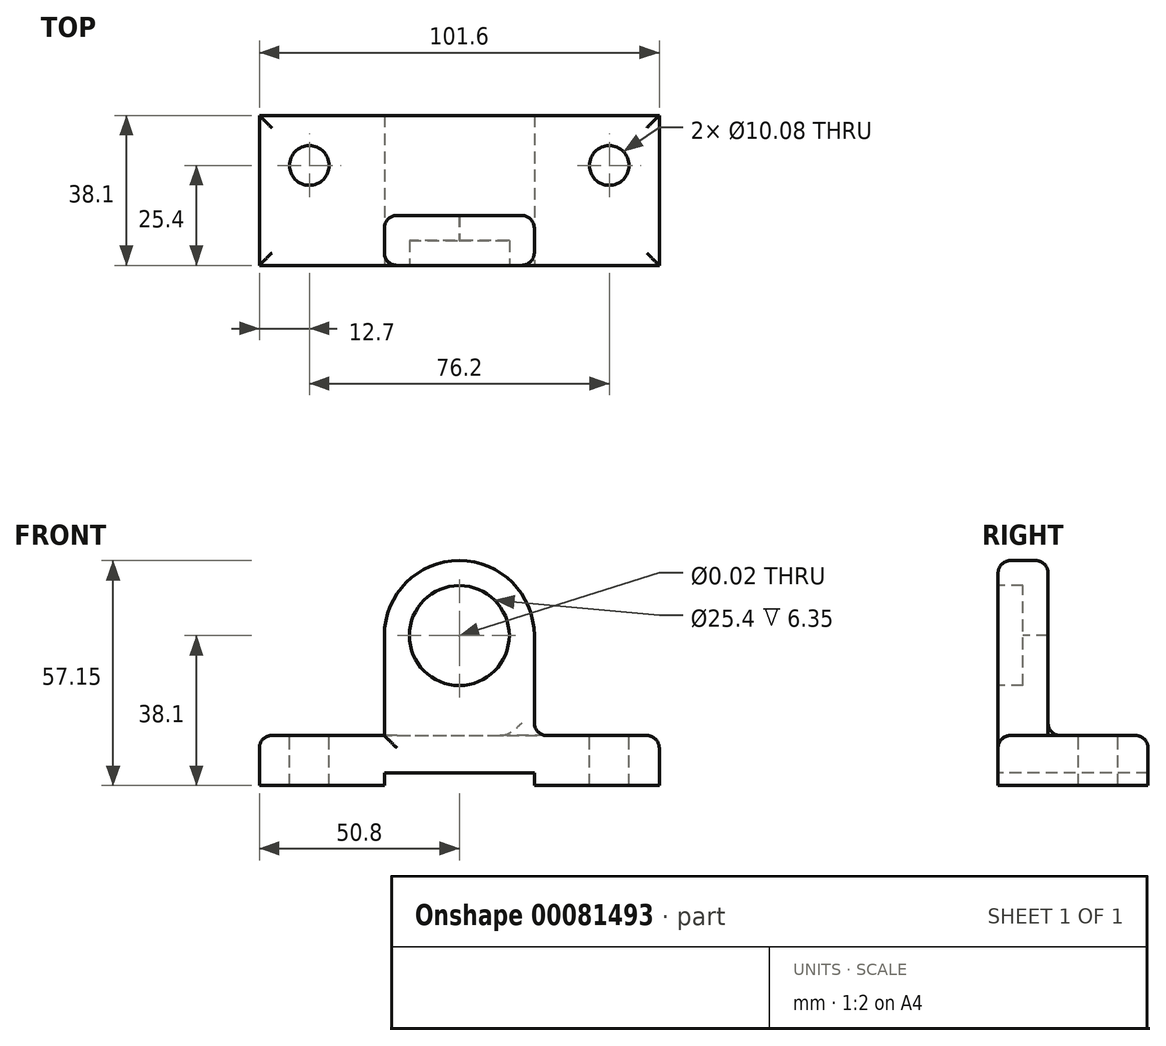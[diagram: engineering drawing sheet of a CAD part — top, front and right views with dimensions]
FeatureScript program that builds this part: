
annotation { "Feature Type Name" : "Feature", "Feature Type Description" : "" }
export const myFeature = defineFeature(function(context is Context, id is Id, definition is map)
    precondition{}
    {
        {
            var Q0;
            Q0=qCreatedBy(makeId("Top.planeOp"),FACE);
            var sketch = newSketch(context, id + "F0", { "sketchPlane" : qUnion([Q0])});
            skLineSegment(sketch, "E0.bottom", {"start": v(0, 0) * mm, "end": v(101.6, 0) * mm});
            skLineSegment(sketch, "E0.top", {"start": v(0, 38.1) * mm, "end": v(101.6, 38.1) * mm});
            skLineSegment(sketch, "E0.left", {"start": v(0, 0) * mm, "end": v(0, 38.1) * mm});
            skLineSegment(sketch, "E0.right", {"start": v(101.6, 0) * mm, "end": v(101.6, 38.1) * mm});
            skSolve(sketch);
        }
        {
            var Q0;
            Q0 = qSketchRegion(id + "F0", true);
            extrude(context, id + "F1", {"entities" : qUnion([Q0]), "depth" : 12.7 * mm});
        }
        {
            var Q0;
            Q0=qCreatedBy(makeId("Front.planeOp"),FACE);
            var sketch = newSketch(context, id + "F2", { "sketchPlane" : qUnion([Q0])});
            skLineSegment(sketch, "E1", {"start": v(0, 0) * mm, "end": v(50.8, 0) * mm});
            skLineSegment(sketch, "E2", {"start": v(0, 0) * mm, "end": v(31.75, 0) * mm});
            skLineSegment(sketch, "E3.bottom", {"start": v(31.75, 0) * mm, "end": v(69.85, 0) * mm});
            skLineSegment(sketch, "E3.top", {"start": v(31.75, 38.1) * mm, "end": v(69.85, 38.1) * mm});
            skLineSegment(sketch, "E3.left", {"start": v(31.75, 0) * mm, "end": v(31.75, 38.1) * mm});
            skLineSegment(sketch, "E3.right", {"start": v(69.85, 0) * mm, "end": v(69.85, 38.1) * mm});
            skLineSegment(sketch, "E4", {"start": v(31.75, 38.1) * mm, "end": v(50.8, 38.1) * mm});
            skArc(sketch, "E5", {"start": v(69.85, 38.1) * mm, "mid": v(50.8, 57.15) * mm, "end": v(31.75, 38.1) * mm});
            skSolve(sketch);
        }
        {
            var Q0;
            Q0 = qSketchRegion(id + "F2", true);
            extrude(context, id + "F3", {"entities" : qUnion([Q0]), "operationType" : NewBodyOperationType.ADD, "oppositeDirection" : true, "depth" : 12.7 * mm});
        }
        {
            var Q0;
            Q0=makeQuery(id+"F3.boolean.opBoolean","MERGE",FACE,{"derivedFrom":[makeQuery(id+"F1.opExtrude","SWEPT_FACE",FACE,{"disambiguationData":[OSD([sQuery(id+"F0.wireOp",EDGE,"E0.bottom")])]}),makeQuery(id+"F3.opExtrude","CAP_FACE",FACE,{"disambiguationData":[OSD([sQuery(id+"F2.wireOp",EDGE,"E3.bottom"),sQuery(id+"F2.wireOp",EDGE,"E3.left"),sQuery(id+"F2.wireOp",EDGE,"E3.right"),sQuery(id+"F2.wireOp",EDGE,"E5")])],"isStart":true})]});
            var sketch = newSketch(context, id + "F4", { "sketchPlane" : qUnion([Q0])});
            skCircle(sketch, "E6", {"center": v(50.8, 38.1) * mm, "radius": 10.13 * mm});
            skSolve(sketch);
        }
        {
            var Q0;
            Q0=sQuery(id+"F4.wireOp",VERTEX,"E6.center");
            var Q1;
            Q1=makeQuery(id+"F1.opExtrude","SWEPT_BODY",BODY,{"disambiguationData":[OSD([sQuery(id+"F0.wireOp",EDGE,"E0.bottom"),sQuery(id+"F0.wireOp",EDGE,"E0.top"),sQuery(id+"F0.wireOp",EDGE,"E0.left"),sQuery(id+"F0.wireOp",EDGE,"E0.right")])]});
            hole(context, id + "F5", {"style" : HoleStyle.C_BORE, "endStyle" : HoleEndStyle.THROUGH, "standardTappedOrClearance" : lookupTablePath({ "standard" : "ANSI", "size" : "15/32 (0.47)", "type" : "Drilled" }), "standardBlindInLast" : lookupTablePath({ "standard" : "ANSI", "size" : "15/32", "type" : "Drilled" }), "holeDiameter" : 15 / 812.8 * mm, "cBoreDiameter" : 25.4 * mm, "cBoreDepth" : 6.35 * mm, "startFromSketch" : true, "locations" : qUnion([Q0]), "scope" : qUnion([Q1]), "isTappedThrough" : true});
        }
        {
            var Q0;
            Q0=makeQuery(id+"F3.boolean.opBoolean","MERGE",FACE,{"derivedFrom":[makeQuery(id+"F1.opExtrude","SWEPT_FACE",FACE,{"disambiguationData":[OSD([sQuery(id+"F0.wireOp",EDGE,"E0.bottom")])]}),makeQuery(id+"F3.opExtrude","CAP_FACE",FACE,{"disambiguationData":[OSD([sQuery(id+"F2.wireOp",EDGE,"E3.bottom"),sQuery(id+"F2.wireOp",EDGE,"E3.left"),sQuery(id+"F2.wireOp",EDGE,"E3.right"),sQuery(id+"F2.wireOp",EDGE,"E5")])],"isStart":true})]});
            var sketch = newSketch(context, id + "F6", { "sketchPlane" : qUnion([Q0])});
            skLineSegment(sketch, "E7.bottom", {"start": v(31.75, 12.7) * mm, "end": v(69.85, 12.7) * mm});
            skLineSegment(sketch, "E7.top", {"start": v(31.75, 0) * mm, "end": v(69.85, 0) * mm});
            skLineSegment(sketch, "E7.left", {"start": v(31.75, 12.7) * mm, "end": v(31.75, 0) * mm});
            skLineSegment(sketch, "E7.right", {"start": v(69.85, 12.7) * mm, "end": v(69.85, 0) * mm});
            skLineSegment(sketch, "E8.top", {"start": v(31.75, 3.17) * mm, "end": v(69.85, 3.17) * mm});
            skLineSegment(sketch, "E8.left", {"start": v(31.75, 0) * mm, "end": v(31.75, 3.17) * mm});
            skLineSegment(sketch, "E8.right", {"start": v(69.85, 0) * mm, "end": v(69.85, 3.17) * mm});
            skSolve(sketch);
        }
        {
            var Q0;
            Q0=makeQuery(id+"F6.imprint","IMPRINT",FACE,{"disambiguationData":[TD([[makeQuery(id+"F6.imprint","IMPRINT",EDGE,{"derivedFrom":sQuery(id+"F6.wireOp",EDGE,"E7.top")}),1.0]])]});
            extrude(context, id + "F7", {"entities" : qUnion([Q0]), "operationType" : NewBodyOperationType.REMOVE, "oppositeDirection" : true, "depth" : 101.6 * mm});
        }
        {
            var Q0;
            Q0=makeQuery(id+"F1.opExtrude","CAP_FACE",FACE,{"disambiguationData":[OSD([sQuery(id+"F0.wireOp",EDGE,"E0.bottom"),sQuery(id+"F0.wireOp",EDGE,"E0.top"),sQuery(id+"F0.wireOp",EDGE,"E0.left"),sQuery(id+"F0.wireOp",EDGE,"E0.right")])],"isStart":false});
            var sketch = newSketch(context, id + "F8", { "sketchPlane" : qUnion([Q0])});
            skLineSegment(sketch, "E9.bottom", {"start": v(0, 38.1) * mm, "end": v(12.7, 38.1) * mm});
            skLineSegment(sketch, "E9.top", {"start": v(0, 25.4) * mm, "end": v(12.7, 25.4) * mm});
            skLineSegment(sketch, "E9.left", {"start": v(0, 38.1) * mm, "end": v(0, 25.4) * mm});
            skLineSegment(sketch, "E9.right", {"start": v(12.7, 38.1) * mm, "end": v(12.7, 25.4) * mm});
            skLineSegment(sketch, "E10.bottom", {"start": v(101.6, 38.1) * mm, "end": v(88.9, 38.1) * mm});
            skLineSegment(sketch, "E10.top", {"start": v(101.6, 25.4) * mm, "end": v(88.9, 25.4) * mm});
            skLineSegment(sketch, "E10.left", {"start": v(101.6, 38.1) * mm, "end": v(101.6, 25.4) * mm});
            skLineSegment(sketch, "E10.right", {"start": v(88.9, 38.1) * mm, "end": v(88.9, 25.4) * mm});
            skSolve(sketch);
        }
        {
            var Q0;
            Q0=sQuery(id+"F8.wireOp",VERTEX,"E9.right.end");
            var Q1;
            Q1=makeQuery(id+"F1.opExtrude","SWEPT_BODY",BODY,{"disambiguationData":[OSD([sQuery(id+"F0.wireOp",EDGE,"E0.bottom"),sQuery(id+"F0.wireOp",EDGE,"E0.top"),sQuery(id+"F0.wireOp",EDGE,"E0.left"),sQuery(id+"F0.wireOp",EDGE,"E0.right")])]});
            hole(context, id + "F9", {"style" : HoleStyle.SIMPLE, "endStyle" : HoleEndStyle.THROUGH, "standardTappedOrClearance" : lookupTablePath({ "standard" : "ANSI", "fit" : "Normal (ASME)", "size" : "3/8", "type" : "Clearance" }), "standardBlindInLast" : lookupTablePath({ "fit" : "Free", "standard" : "ANSI", "size" : "3/8", "type" : "Clearance" }), "holeDiameter" : 10.08 * mm, "startFromSketch" : true, "locations" : qUnion([Q0]), "scope" : qUnion([Q1]), "isTappedThrough" : true});
        }
        {
            var Q0;
            Q0=sQuery(id+"F8.wireOp",VERTEX,"E10.top.end");
            var Q1;
            Q1=makeQuery(id+"F1.opExtrude","SWEPT_BODY",BODY,{"disambiguationData":[OSD([sQuery(id+"F0.wireOp",EDGE,"E0.bottom"),sQuery(id+"F0.wireOp",EDGE,"E0.top"),sQuery(id+"F0.wireOp",EDGE,"E0.left"),sQuery(id+"F0.wireOp",EDGE,"E0.right")])]});
            hole(context, id + "F10", {"style" : HoleStyle.SIMPLE, "endStyle" : HoleEndStyle.THROUGH, "standardTappedOrClearance" : lookupTablePath({ "standard" : "ANSI", "fit" : "Normal (ASME)", "size" : "3/8", "type" : "Clearance" }), "standardBlindInLast" : lookupTablePath({ "fit" : "Free", "standard" : "ANSI", "size" : "3/8", "type" : "Clearance" }), "holeDiameter" : 10.08 * mm, "startFromSketch" : true, "locations" : qUnion([Q0]), "scope" : qUnion([Q1]), "isTappedThrough" : true});
        }
        {
            var Q0;
            Q0=makeQuery(id+"F3.opExtrude","CAP_EDGE",EDGE,{"disambiguationData":[OSD([sQuery(id+"F2.wireOp",EDGE,"E3.right")])],"isStart":true});
            var Q1;
            {var subQ0=sQuery(id+"F0.wireOp",EDGE,"E0.right");var subQ1=sQuery(id+"F0.wireOp",EDGE,"E0.bottom");Q1=makeQuery(id+"F3.boolean.opBoolean","SPLIT",EDGE,{"disambiguationData":[TD([makeQuery(id+"F1.opExtrude","SWEPT_FACE",FACE,{"disambiguationData":[OSD([subQ0])]})])],"derivedFrom":makeQuery(id+"F1.opExtrude","CAP_EDGE",EDGE,{"disambiguationData":[OSD([subQ1])],"isStart":false})});}
            var Q2;
            {var subQ0=sQuery(id+"F0.wireOp",EDGE,"E0.left");var subQ2=sQuery(id+"F0.wireOp",EDGE,"E0.bottom");Q2=makeQuery(id+"F3.boolean.opBoolean","SPLIT",EDGE,{"disambiguationData":[TD([makeQuery(id+"F1.opExtrude","SWEPT_FACE",FACE,{"disambiguationData":[OSD([subQ0])]})])],"derivedFrom":makeQuery(id+"F1.opExtrude","CAP_EDGE",EDGE,{"disambiguationData":[OSD([subQ2])],"isStart":false})});}
            var Q3;
            Q3=makeQuery(id+"F1.opExtrude","CAP_EDGE",EDGE,{"disambiguationData":[OSD([sQuery(id+"F0.wireOp",EDGE,"E0.left")])],"isStart":false});
            var Q4;
            Q4=makeQuery(id+"F1.opExtrude","CAP_EDGE",EDGE,{"disambiguationData":[OSD([sQuery(id+"F0.wireOp",EDGE,"E0.top")])],"isStart":false});
            var Q5;
            Q5=makeQuery(id+"F1.opExtrude","CAP_EDGE",EDGE,{"disambiguationData":[OSD([sQuery(id+"F0.wireOp",EDGE,"E0.right")])],"isStart":false});
            var Q6;
            Q6=makeQuery(id+"F3.boolean.opBoolean","INTERSECT",EDGE,{"derivedFrom":[makeQuery(id+"F1.opExtrude","CAP_FACE",FACE,{"disambiguationData":[OSD([sQuery(id+"F0.wireOp",EDGE,"E0.bottom"),sQuery(id+"F0.wireOp",EDGE,"E0.top"),sQuery(id+"F0.wireOp",EDGE,"E0.left"),sQuery(id+"F0.wireOp",EDGE,"E0.right")])],"isStart":false}),makeQuery(id+"F3.opExtrude","SWEPT_FACE",FACE,{"disambiguationData":[OSD([sQuery(id+"F2.wireOp",EDGE,"E3.right")])]})]});
            var Q7;
            Q7=makeQuery(id+"F3.opExtrude","CAP_EDGE",EDGE,{"disambiguationData":[OSD([sQuery(id+"F2.wireOp",EDGE,"E3.right")])],"isStart":false});
            fillet(context, id + "F11", {"entities" : qUnion([Q0, Q1, Q2, Q3, Q4, Q5, Q6, Q7]), "radius" : 3.17 * mm, "tangentPropagation" : true, "allowEdgeOverflow" : false});
        }
    });
